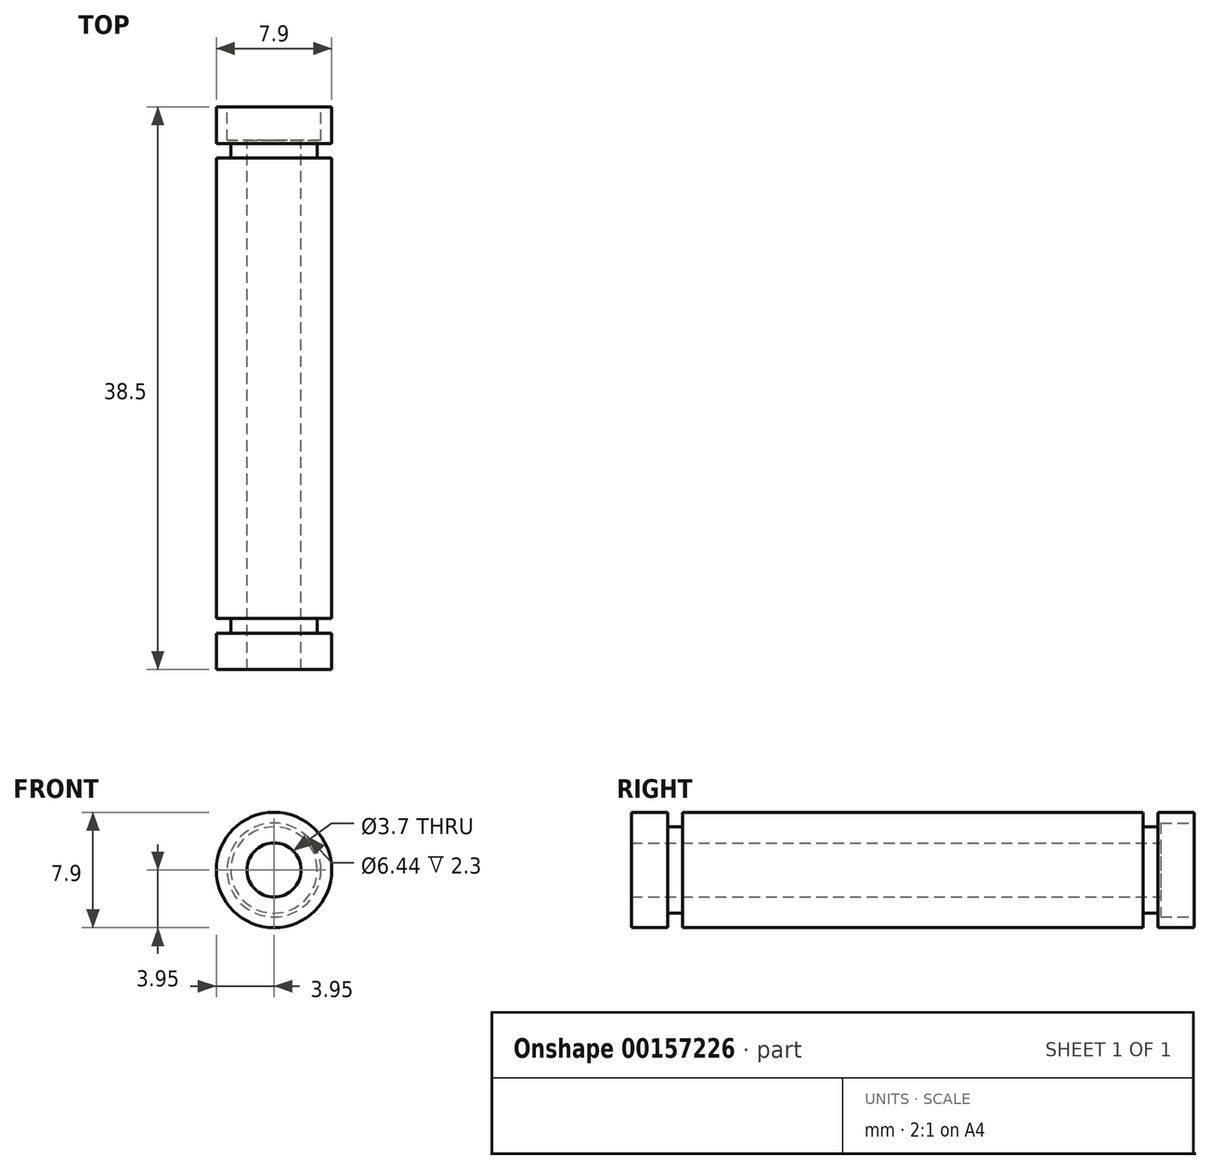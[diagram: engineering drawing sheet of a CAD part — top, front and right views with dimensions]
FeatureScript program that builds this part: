
annotation { "Feature Type Name" : "Feature", "Feature Type Description" : "" }
export const myFeature = defineFeature(function(context is Context, id is Id, definition is map)
    precondition{}
    {
        {
            var Q0;
            Q0=qCreatedBy(makeId("Right.planeOp"),FACE);
            var sketch = newSketch(context, id + "F0", { "sketchPlane" : qUnion([Q0])});
            skLineSegment(sketch, "E0", {"start": v(11.47, 0) * mm, "end": v(0, 0) * mm, "construction": true});
            skLineSegment(sketch, "E1", {"start": v(36.2, 1.85) * mm, "end": v(0, 1.85) * mm});
            skLineSegment(sketch, "E2", {"start": v(36.2, 1.85) * mm, "end": v(36.2, 3.22) * mm});
            skLineSegment(sketch, "E3", {"start": v(38.5, 3.22) * mm, "end": v(36.2, 3.22) * mm});
            skLineSegment(sketch, "E4", {"start": v(38.5, 3.22) * mm, "end": v(38.5, 3.95) * mm});
            skLineSegment(sketch, "E5", {"start": v(36, 3.95) * mm, "end": v(38.5, 3.95) * mm});
            skLineSegment(sketch, "E6", {"start": v(36, 3.95) * mm, "end": v(36, 2.95) * mm});
            skLineSegment(sketch, "E7", {"start": v(35, 2.95) * mm, "end": v(36, 2.95) * mm});
            skLineSegment(sketch, "E8", {"start": v(2.5, 2.95) * mm, "end": v(2.5, 3.95) * mm});
            skLineSegment(sketch, "E9", {"start": v(0, 3.95) * mm, "end": v(2.5, 3.95) * mm});
            skLineSegment(sketch, "E10", {"start": v(0, 3.95) * mm, "end": v(0, 1.85) * mm});
            skLineSegment(sketch, "E11", {"start": v(3.5, 2.95) * mm, "end": v(3.5, 3.95) * mm});
            skLineSegment(sketch, "E12", {"start": v(3.5, 3.95) * mm, "end": v(35, 3.95) * mm});
            skLineSegment(sketch, "E13", {"start": v(35, 3.95) * mm, "end": v(35, 2.95) * mm});
            skLineSegment(sketch, "E14.trimOffspring", {"start": v(3.5, 2.95) * mm, "end": v(2.5, 2.95) * mm});
            skSolve(sketch);
        }
        {
            var Q0;
            Q0=makeQuery(id+"F0.imprint","IMPRINT",FACE,{"disambiguationData":[TD([[makeQuery(id+"F0.imprint","IMPRINT",EDGE,{"derivedFrom":sQuery(id+"F0.wireOp",EDGE,"E1")}),-1.0]])]});
            var Q1;
            Q1=sQuery(id+"F0.wireOp",EDGE,"E0");
            revolve(context, id + "F1", {"entities" : qUnion([Q0]), "axis" : qUnion([Q1]), "revolveType" : RevolveType.FULL});
        }
    });
